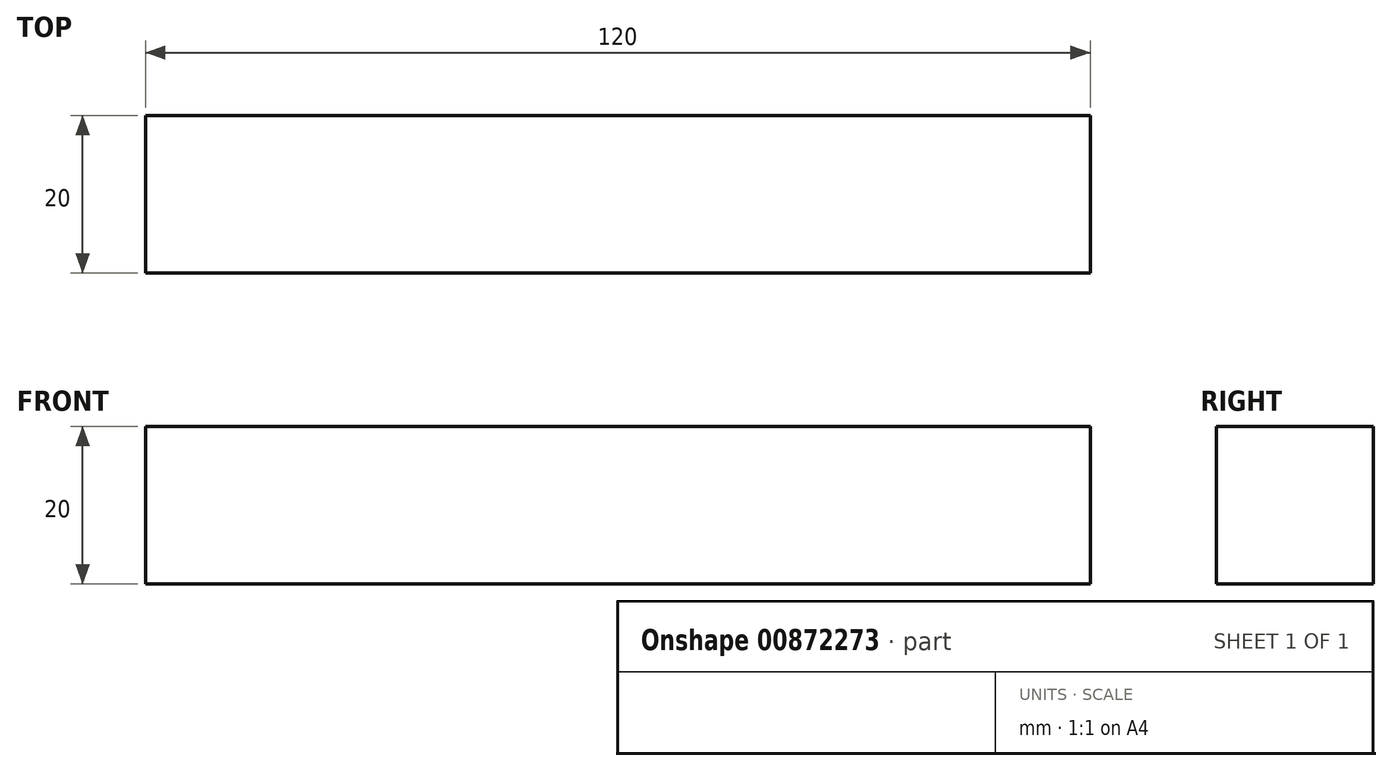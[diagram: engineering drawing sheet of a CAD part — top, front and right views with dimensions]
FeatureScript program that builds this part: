
annotation { "Feature Type Name" : "Feature", "Feature Type Description" : "" }
export const myFeature = defineFeature(function(context is Context, id is Id, definition is map)
    precondition{}
    {
        {
            var Q0;
            Q0=qCreatedBy(makeId("Front.planeOp"),FACE);
            var sketch = newSketch(context, id + "F0", { "sketchPlane" : qUnion([Q0])});
            skLineSegment(sketch, "E0.bottom", {"start": v(60, -10) * mm, "end": v(-60, -10) * mm});
            skLineSegment(sketch, "E0.top", {"start": v(60, 10) * mm, "end": v(-60, 10) * mm});
            skLineSegment(sketch, "E0.left", {"start": v(60, -10) * mm, "end": v(60, 10) * mm});
            skLineSegment(sketch, "E0.right", {"start": v(-60, -10) * mm, "end": v(-60, 10) * mm});
            skPoint(sketch, "E0.middle", {"position": v(0, 0) * mm});
            skSolve(sketch);
        }
        {
            var Q0;
            Q0=makeQuery(id+"F0.imprint","IMPRINT",FACE,{"disambiguationData":[TD([[makeQuery(id+"F0.imprint","IMPRINT",EDGE,{"derivedFrom":sQuery(id+"F0.wireOp",EDGE,"E0.bottom")}),-1.0]])]});
            extrude(context, id + "F1", {"entities" : qUnion([Q0]), "endBound" : BoundingType.SYMMETRIC, "depth" : 20 * mm, "offsetDistance" : 25 * mm});
        }
    });
